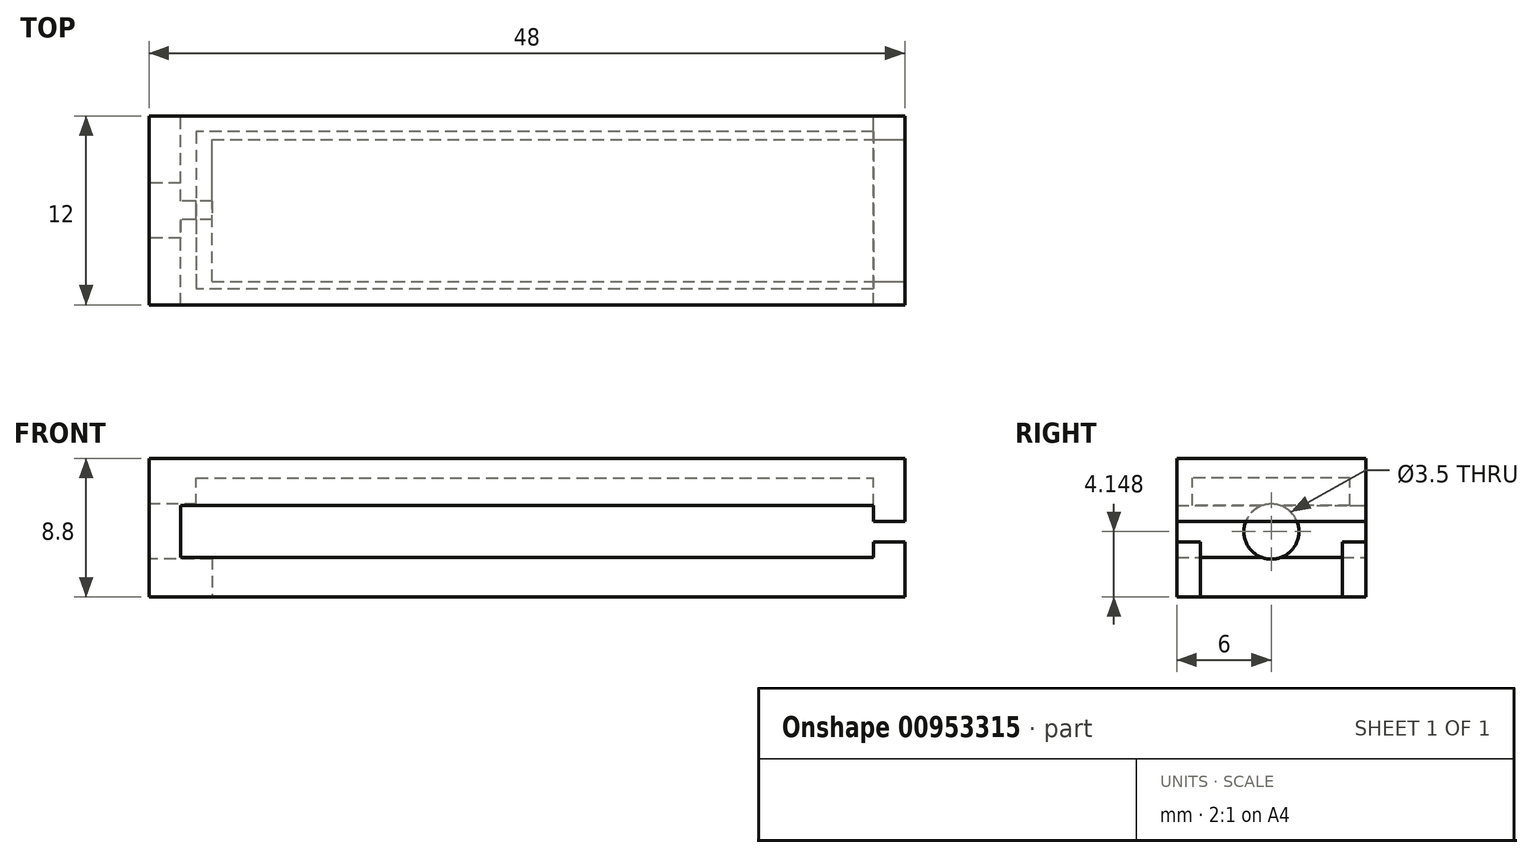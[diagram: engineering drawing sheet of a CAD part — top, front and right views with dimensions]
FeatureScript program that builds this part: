
annotation { "Feature Type Name" : "Feature", "Feature Type Description" : "" }
export const myFeature = defineFeature(function(context is Context, id is Id, definition is map)
    precondition{}
    {
        {
            var Q0;
            Q0=qCreatedBy(makeId("Front.planeOp"),FACE);
            var sketch = newSketch(context, id + "F0", { "sketchPlane" : qUnion([Q0])});
            skLineSegment(sketch, "E0.bottom", {"start": v(-18.3, -5.28) * mm, "end": v(29.7, -5.28) * mm});
            skLineSegment(sketch, "E0.top", {"start": v(-18.3, -14.08) * mm, "end": v(29.7, -14.08) * mm});
            skLineSegment(sketch, "E0.left", {"start": v(-18.3, -5.28) * mm, "end": v(-18.3, -14.08) * mm});
            skLineSegment(sketch, "E1", {"start": v(-16.3, -8.28) * mm, "end": v(27.7, -8.28) * mm});
            skLineSegment(sketch, "E2", {"start": v(-16.3, -8.28) * mm, "end": v(-16.3, -11.58) * mm});
            skLineSegment(sketch, "E3", {"start": v(-16.3, -11.58) * mm, "end": v(27.7, -11.58) * mm});
            skLineSegment(sketch, "E4", {"start": v(27.7, -8.28) * mm, "end": v(27.7, -9.28) * mm});
            skLineSegment(sketch, "E5", {"start": v(27.7, -9.28) * mm, "end": v(29.7, -9.28) * mm});
            skLineSegment(sketch, "E6", {"start": v(29.7, -5.28) * mm, "end": v(29.7, -9.28) * mm});
            skLineSegment(sketch, "E7", {"start": v(27.7, -11.58) * mm, "end": v(27.7, -10.58) * mm});
            skLineSegment(sketch, "E8", {"start": v(27.7, -10.58) * mm, "end": v(29.7, -10.58) * mm});
            skLineSegment(sketch, "E9", {"start": v(29.7, -10.58) * mm, "end": v(29.7, -14.08) * mm});
            skSolve(sketch);
        }
        {
            var Q0;
            Q0=makeQuery(id+"F0.imprint","IMPRINT",FACE,{"disambiguationData":[TD([[makeQuery(id+"F0.imprint","IMPRINT",EDGE,{"derivedFrom":sQuery(id+"F0.wireOp",EDGE,"E0.bottom")}),-1.0]])]});
            extrude(context, id + "F1", {"entities" : qUnion([Q0]), "depth" : 12 * mm, "offsetDistance" : 25 * mm});
        }
        {
            var Q0;
            Q0=makeQuery(id+"F1.opExtrude","SWEPT_FACE",FACE,{"disambiguationData":[OSD([sQuery(id+"F0.wireOp",EDGE,"E4")])]});
            cPlane(context, id + "F2", {"entities" : qUnion([Q0]), "cplaneType" : CPlaneType.OFFSET, "offset" : 0 * mm, "width" : 150 * mm, "height" : 150 * mm});
        }
        {
            var Q0;
            Q0=qCreatedBy(id+"F2.planeOp",FACE);
            var sketch = newSketch(context, id + "F3", { "sketchPlane" : qUnion([Q0])});
            skLineSegment(sketch, "E10.bottom", {"start": v(1, -8.53) * mm, "end": v(11, -8.53) * mm});
            skLineSegment(sketch, "E10.top", {"start": v(1, -6.53) * mm, "end": v(11, -6.53) * mm});
            skLineSegment(sketch, "E10.left", {"start": v(1, -8.53) * mm, "end": v(1, -6.53) * mm});
            skLineSegment(sketch, "E10.right", {"start": v(11, -8.53) * mm, "end": v(11, -6.53) * mm});
            skSolve(sketch);
        }
        {
            var Q0;
            Q0 = qSketchRegion(id + "F3", true);
            extrude(context, id + "F4", {"entities" : qUnion([Q0]), "operationType" : NewBodyOperationType.REMOVE, "depth" : 43 * mm, "offsetDistance" : 25 * mm});
        }
        {
            var Q0;
            Q0=makeQuery(id+"F1.opExtrude","SWEPT_FACE",FACE,{"disambiguationData":[OSD([sQuery(id+"F0.wireOp",EDGE,"E9")])]});
            cPlane(context, id + "F5", {"entities" : qUnion([Q0]), "cplaneType" : CPlaneType.OFFSET, "offset" : 25 * mm, "width" : 150 * mm, "height" : 150 * mm});
        }
        {
            var Q0;
            Q0=qCreatedBy(id+"F5.planeOp",FACE);
            var sketch = newSketch(context, id + "F6", { "sketchPlane" : qUnion([Q0])});
            skLineSegment(sketch, "E11.bottom", {"start": v(-10.5, -10.55) * mm, "end": v(-1.5, -10.55) * mm});
            skLineSegment(sketch, "E11.top", {"start": v(-10.5, -15.3) * mm, "end": v(-1.5, -15.3) * mm});
            skLineSegment(sketch, "E11.left", {"start": v(-10.5, -10.55) * mm, "end": v(-10.5, -15.3) * mm});
            skLineSegment(sketch, "E11.right", {"start": v(-1.5, -10.55) * mm, "end": v(-1.5, -15.3) * mm});
            skSolve(sketch);
        }
        {
            var Q0;
            Q0=makeQuery(id+"F6.imprint","IMPRINT",FACE,{"disambiguationData":[TD([[makeQuery(id+"F6.imprint","IMPRINT",EDGE,{"derivedFrom":sQuery(id+"F6.wireOp",EDGE,"E11.bottom")}),-1.0]])]});
            extrude(context, id + "F7", {"entities" : qUnion([Q0]), "operationType" : NewBodyOperationType.REMOVE, "oppositeDirection" : true, "depth" : 69 * mm, "offsetDistance" : 25 * mm});
        }
        {
            var Q0;
            Q0=makeQuery(id+"F1.opExtrude","SWEPT_FACE",FACE,{"disambiguationData":[OSD([sQuery(id+"F0.wireOp",EDGE,"E0.left")])]});
            var sketch = newSketch(context, id + "F8", { "sketchPlane" : qUnion([Q0])});
            skPoint(sketch, "E12", {"position": v(6, -9.93) * mm});
            skSolve(sketch);
        }
        {
            var Q0;
            Q0=sQuery(id+"F8.wireOp",VERTEX,"E12");
            var Q1;
            Q1=makeQuery(id+"F1.opExtrude","SWEPT_BODY",BODY,{"disambiguationData":[OSD([sQuery(id+"F0.wireOp",EDGE,"E0.bottom"),sQuery(id+"F0.wireOp",EDGE,"E0.top"),sQuery(id+"F0.wireOp",EDGE,"E0.left"),sQuery(id+"F0.wireOp",EDGE,"E1"),sQuery(id+"F0.wireOp",EDGE,"E2"),sQuery(id+"F0.wireOp",EDGE,"E3"),sQuery(id+"F0.wireOp",EDGE,"E4"),sQuery(id+"F0.wireOp",EDGE,"E5"),sQuery(id+"F0.wireOp",EDGE,"E6"),sQuery(id+"F0.wireOp",EDGE,"E7"),sQuery(id+"F0.wireOp",EDGE,"E8"),sQuery(id+"F0.wireOp",EDGE,"E9")])]});
            hole(context, id + "F9", {"style" : HoleStyle.SIMPLE, "endStyle" : HoleEndStyle.BLIND, "holeDiameter" : 3.5 * mm, "majorDiameter" : 5 * mm, "holeDepth" : 4 * mm, "isTappedThrough" : true, "tappedDepth" : 12 * mm, "tapClearance" : 3, "locations" : qUnion([Q0]), "scope" : qUnion([Q1])});
        }
    });
